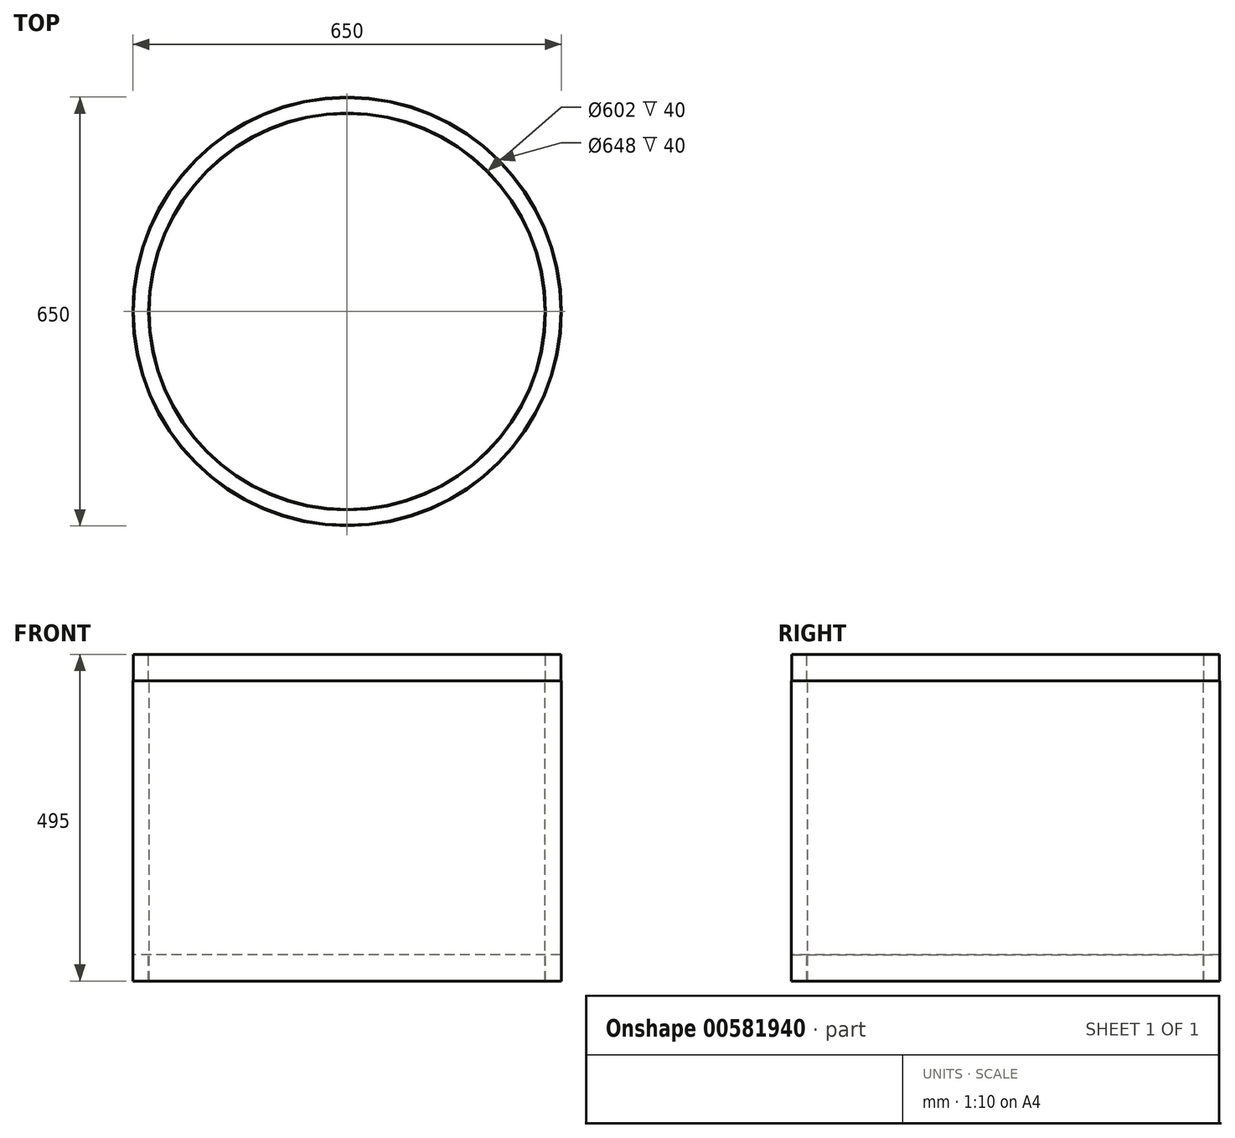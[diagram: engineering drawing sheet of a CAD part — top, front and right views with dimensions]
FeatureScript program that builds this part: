
annotation { "Feature Type Name" : "Feature", "Feature Type Description" : "" }
export const myFeature = defineFeature(function(context is Context, id is Id, definition is map)
    precondition{}
    {
        {
            var Q0;
            Q0=qCreatedBy(makeId("Front.planeOp"),FACE);
            var sketch = newSketch(context, id + "F0", { "sketchPlane" : qUnion([Q0])});
            skLineSegment(sketch, "E0", {"start": v(0, 345.75) * mm, "end": v(0, -558.03) * mm, "construction": true});
            skLineSegment(sketch, "E1", {"start": v(-300, -518.84) * mm, "end": v(-300, -63.84) * mm});
            skLineSegment(sketch, "E2", {"start": v(-300, -63.84) * mm, "end": v(-301, -63.84) * mm});
            skLineSegment(sketch, "E3", {"start": v(-301, -63.84) * mm, "end": v(-301, -23.84) * mm});
            skLineSegment(sketch, "E4", {"start": v(-301, -23.84) * mm, "end": v(-324, -23.84) * mm});
            skLineSegment(sketch, "E5", {"start": v(-324, -23.84) * mm, "end": v(-324, -63.84) * mm});
            skLineSegment(sketch, "E6", {"start": v(-324, -63.84) * mm, "end": v(-325, -63.84) * mm});
            skLineSegment(sketch, "E7", {"start": v(-325, -63.84) * mm, "end": v(-325, -518.84) * mm});
            skLineSegment(sketch, "E8", {"start": v(-325, -518.84) * mm, "end": v(-324, -518.84) * mm});
            skLineSegment(sketch, "E9", {"start": v(-324, -518.84) * mm, "end": v(-324, -478.84) * mm});
            skLineSegment(sketch, "E10", {"start": v(-324, -478.84) * mm, "end": v(-301, -478.84) * mm});
            skLineSegment(sketch, "E11", {"start": v(-301, -478.84) * mm, "end": v(-301, -518.84) * mm});
            skLineSegment(sketch, "E12", {"start": v(-301, -518.84) * mm, "end": v(-300, -518.84) * mm});
            skSolve(sketch);
        }
        {
            var Q0;
            Q0=qSketchRegion(id+"F0",true);
            var Q1;
            Q1=sQuery(id+"F0.wireOp",EDGE,"E0");
            revolve(context, id + "F1", {"entities" : qUnion([Q0]), "axis" : qUnion([Q1]), "revolveType" : RevolveType.FULL});
        }
    });
